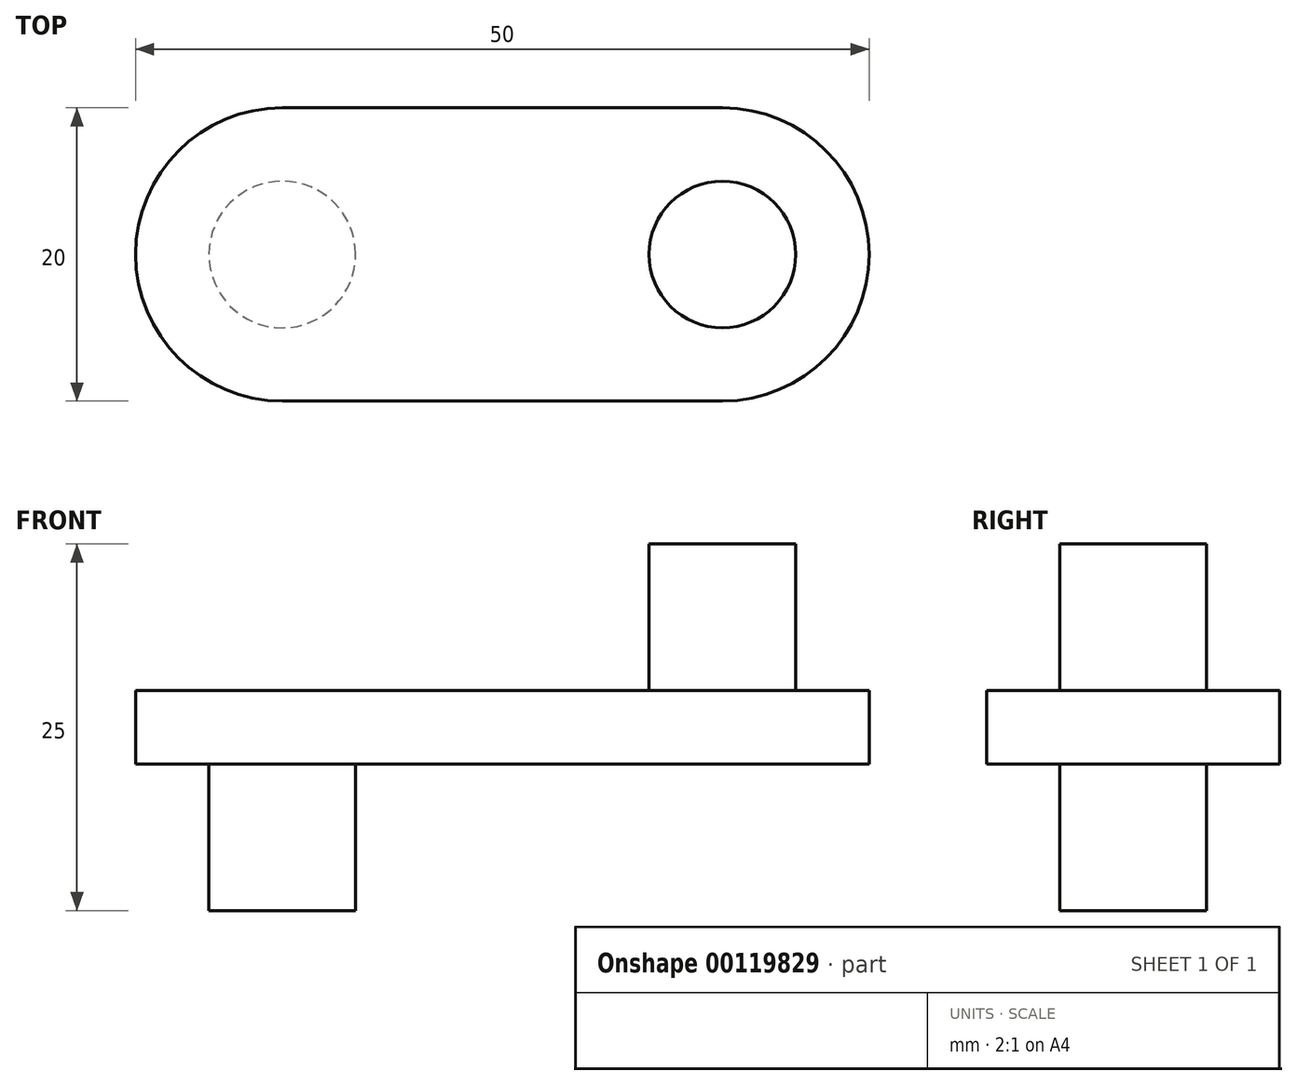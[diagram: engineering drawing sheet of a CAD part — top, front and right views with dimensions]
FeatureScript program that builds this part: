
annotation { "Feature Type Name" : "Feature", "Feature Type Description" : "" }
export const myFeature = defineFeature(function(context is Context, id is Id, definition is map)
    precondition{}
    {
        {
            var Q0;
            Q0=qCreatedBy(makeId("Top.planeOp"),FACE);
            var sketch = newSketch(context, id + "F0", { "sketchPlane" : qUnion([Q0])});
            skArc(sketch, "E0", {"start": v(0, 10) * mm, "mid": v(-10, 0) * mm, "end": v(0, -10) * mm});
            skLineSegment(sketch, "E1", {"start": v(0, 10) * mm, "end": v(30, 10) * mm});
            skLineSegment(sketch, "E2", {"start": v(0, -10) * mm, "end": v(30, -10) * mm});
            skArc(sketch, "E3", {"start": v(30, -10) * mm, "mid": v(40, 0) * mm, "end": v(30, 10) * mm});
            skSolve(sketch);
        }
        {
            var Q0;
            Q0=makeQuery(id+"F0.imprint","IMPRINT",FACE,{"disambiguationData":[TD([[makeQuery(id+"F0.imprint","IMPRINT",EDGE,{"derivedFrom":sQuery(id+"F0.wireOp",EDGE,"E0")}),1.0]])]});
            extrude(context, id + "F1", {"entities" : qUnion([Q0]), "oppositeDirection" : true, "depth" : 5 * mm});
        }
        {
            var Q0;
            Q0=qCreatedBy(makeId("Top.planeOp"),FACE);
            var sketch = newSketch(context, id + "F2", { "sketchPlane" : qUnion([Q0])});
            skCircle(sketch, "E4", {"center": v(30, 0) * mm, "radius": 5 * mm});
            skSolve(sketch);
        }
        {
            var Q0;
            Q0=qSketchRegion(id+"F2",true);
            extrude(context, id + "F3", {"entities" : qUnion([Q0]), "operationType" : NewBodyOperationType.ADD, "depth" : 10 * mm});
        }
        {
            var Q0;
            Q0=makeQuery(id+"F1.opExtrude","CAP_FACE",FACE,{"disambiguationData":[OSD([sQuery(id+"F0.wireOp",EDGE,"E0"),sQuery(id+"F0.wireOp",EDGE,"E1"),sQuery(id+"F0.wireOp",EDGE,"E2"),sQuery(id+"F0.wireOp",EDGE,"E3")])],"isStart":false});
            var sketch = newSketch(context, id + "F4", { "sketchPlane" : qUnion([Q0])});
            skCircle(sketch, "E5", {"center": v(0, 0) * mm, "radius": 5 * mm});
            skSolve(sketch);
        }
        {
            var Q0;
            Q0 = qSketchRegion(id + "F4", true);
            extrude(context, id + "F5", {"entities" : qUnion([Q0]), "operationType" : NewBodyOperationType.ADD, "depth" : 10 * mm});
        }
    });
